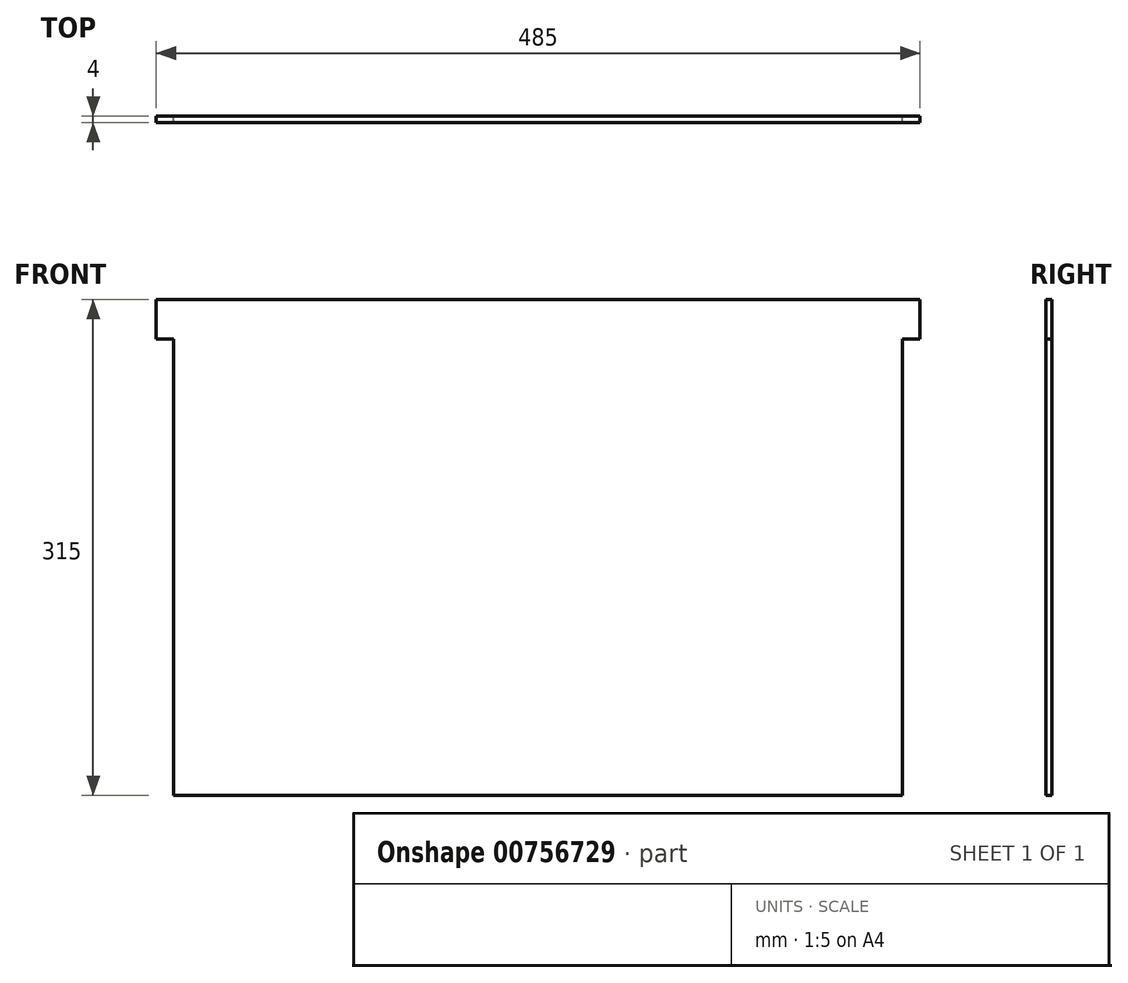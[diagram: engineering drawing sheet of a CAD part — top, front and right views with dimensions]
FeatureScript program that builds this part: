
annotation { "Feature Type Name" : "Feature", "Feature Type Description" : "" }
export const myFeature = defineFeature(function(context is Context, id is Id, definition is map)
    precondition{}
    {
        {
            var Q0;
            Q0=qCreatedBy(makeId("Front.planeOp"),FACE);
            var sketch = newSketch(context, id + "F0", { "sketchPlane" : qUnion([Q0])});
            skLineSegment(sketch, "E0", {"start": v(242.5, 315) * mm, "end": v(-242.5, 315) * mm});
            skLineSegment(sketch, "E1", {"start": v(-242.5, 315) * mm, "end": v(-242.5, 290) * mm});
            skLineSegment(sketch, "E2", {"start": v(-242.5, 290) * mm, "end": v(-231.5, 290) * mm});
            skLineSegment(sketch, "E3", {"start": v(-231.5, 290) * mm, "end": v(-231.5, 0) * mm});
            skLineSegment(sketch, "E4", {"start": v(-231.5, 0) * mm, "end": v(231.5, 0) * mm});
            skLineSegment(sketch, "E5", {"start": v(231.5, 0) * mm, "end": v(231.5, 290) * mm});
            skLineSegment(sketch, "E6", {"start": v(231.5, 290) * mm, "end": v(242.5, 290) * mm});
            skLineSegment(sketch, "E7", {"start": v(242.5, 290) * mm, "end": v(242.5, 315) * mm});
            skSolve(sketch);
        }
        {
            var Q0;
            Q0 = qSketchRegion(id + "F0", true);
            extrude(context, id + "F1", {"entities" : qUnion([Q0]), "depth" : 4 * mm, "offsetDistance" : 25 * mm, "symmetric" : true});
        }
    });
